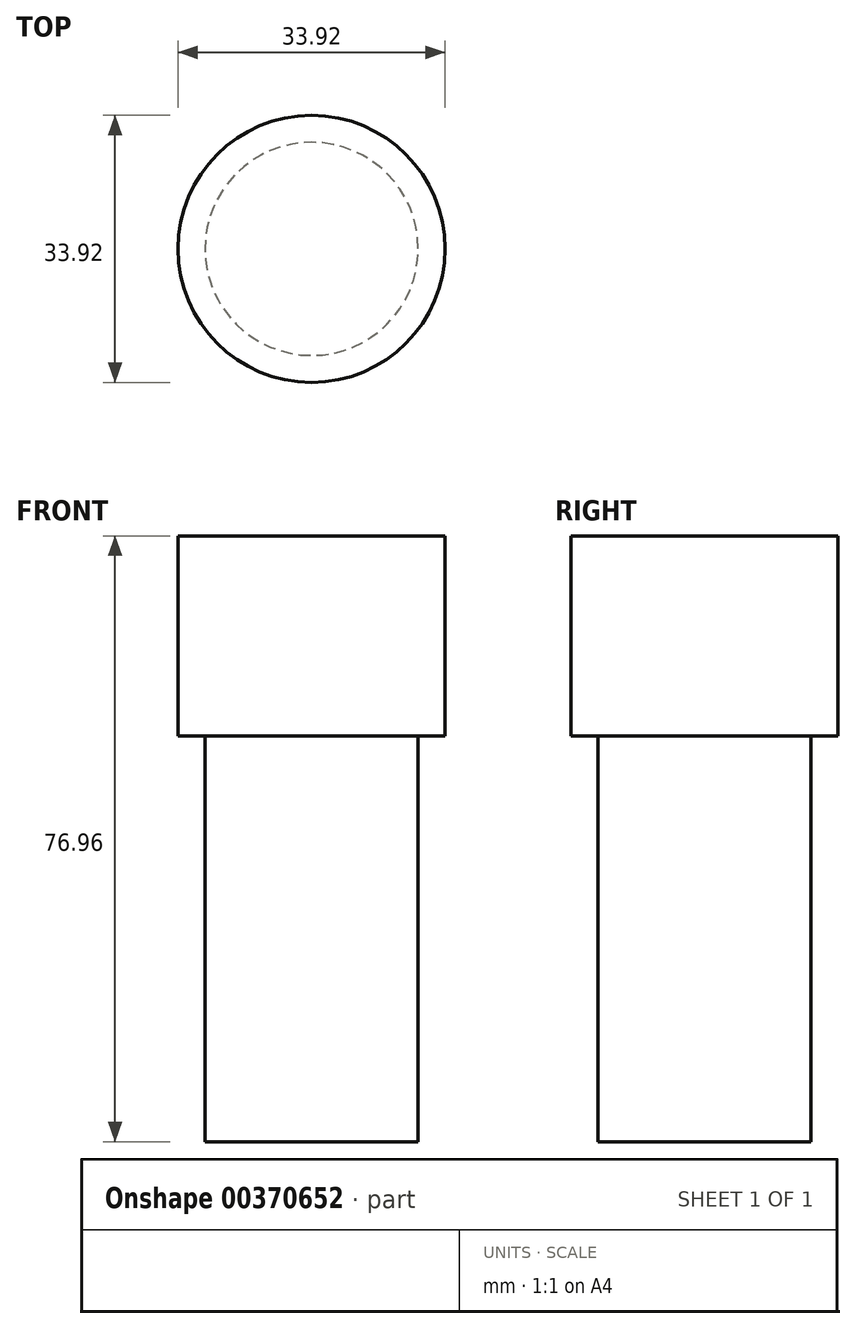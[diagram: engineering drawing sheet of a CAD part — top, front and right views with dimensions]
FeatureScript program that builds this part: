
annotation { "Feature Type Name" : "Feature", "Feature Type Description" : "" }
export const myFeature = defineFeature(function(context is Context, id is Id, definition is map)
    precondition{}
    {
        {
            var Q0;
            Q0=qCreatedBy(makeId("Top.planeOp"),FACE);
            var sketch = newSketch(context, id + "F0", { "sketchPlane" : qUnion([Q0])});
            skCircle(sketch, "E0", {"center": v(0, 0) * mm, "radius": 16.96 * mm});
            skSolve(sketch);
        }
        {
            var Q0;
            Q0=qCreatedBy(makeId("Top.planeOp"),FACE);
            var sketch = newSketch(context, id + "F1", { "sketchPlane" : qUnion([Q0])});
            skCircle(sketch, "E1", {"center": v(0, 0) * mm, "radius": 14.66 * mm});
            skSolve(sketch);
        }
        {
            var Q0;
            Q0=makeQuery(id+"F0.imprint","IMPRINT",FACE,{"disambiguationData":[TD([[makeQuery(id+"F0.imprint","IMPRINT",EDGE,{"derivedFrom":sQuery(id+"F0.wireOp",EDGE,"E0")}),1.0]])]});
            extrude(context, id + "F2", {"entities" : qUnion([Q0]), "depth" : 25.4 * mm});
        }
        {
            var Q0;
            Q0=sQuery(id+"F1.wireOp",EDGE,"E1");
            extrude(context, id + "F3", {"bodyType" : ToolBodyType.SURFACE, "surfaceEntities" : qUnion([Q0]), "depth" : 20.32 * mm});
        }
        {
            var Q0;
            Q0=qCreatedBy(makeId("Top.planeOp"),FACE);
            var sketch = newSketch(context, id + "F4", { "sketchPlane" : qUnion([Q0])});
            skCircle(sketch, "E2", {"center": v(0, 0) * mm, "radius": 13.53 * mm});
            skSolve(sketch);
        }
        {
            var Q0;
            Q0=makeQuery(id+"F4.imprint","IMPRINT",FACE,{"disambiguationData":[TD([[makeQuery(id+"F4.imprint","IMPRINT",EDGE,{"derivedFrom":sQuery(id+"F4.wireOp",EDGE,"E2")}),1.0]])]});
            extrude(context, id + "F5", {"entities" : qUnion([Q0]), "operationType" : NewBodyOperationType.ADD, "depth" : -51.56 * mm});
        }
    });
